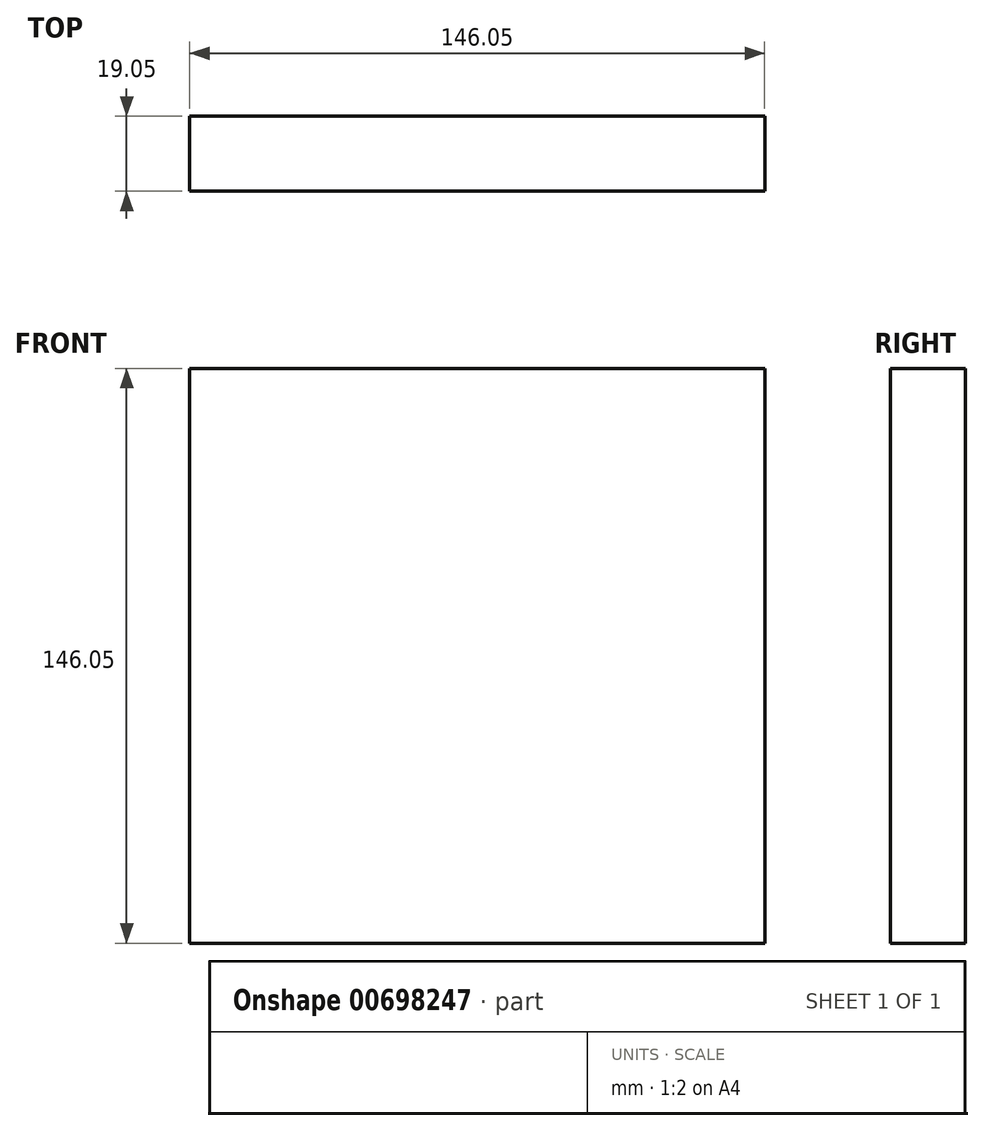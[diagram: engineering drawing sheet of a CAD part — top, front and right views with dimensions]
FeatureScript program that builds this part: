
annotation { "Feature Type Name" : "Feature", "Feature Type Description" : "" }
export const myFeature = defineFeature(function(context is Context, id is Id, definition is map)
    precondition{}
    {
        {
            var Q0;
            Q0=qCreatedBy(makeId("Front.planeOp"),FACE);
            var sketch = newSketch(context, id + "F0", { "sketchPlane" : qUnion([Q0])});
            skLineSegment(sketch, "E0.bottom", {"start": v(-158.25, -97.52) * mm, "end": v(-12.2, -97.52) * mm});
            skLineSegment(sketch, "E0.top", {"start": v(-158.25, 48.53) * mm, "end": v(-12.2, 48.53) * mm});
            skLineSegment(sketch, "E0.left", {"start": v(-158.25, -97.52) * mm, "end": v(-158.25, 48.53) * mm});
            skLineSegment(sketch, "E0.right", {"start": v(-12.2, -97.52) * mm, "end": v(-12.2, 48.53) * mm});
            skSolve(sketch);
        }
        {
            var Q0;
            Q0 = qSketchRegion(id + "F0", true);
            extrude(context, id + "F1", {"entities" : qUnion([Q0]), "depth" : 19.05 * mm, "offsetDistance" : 25.4 * mm});
        }
    });
